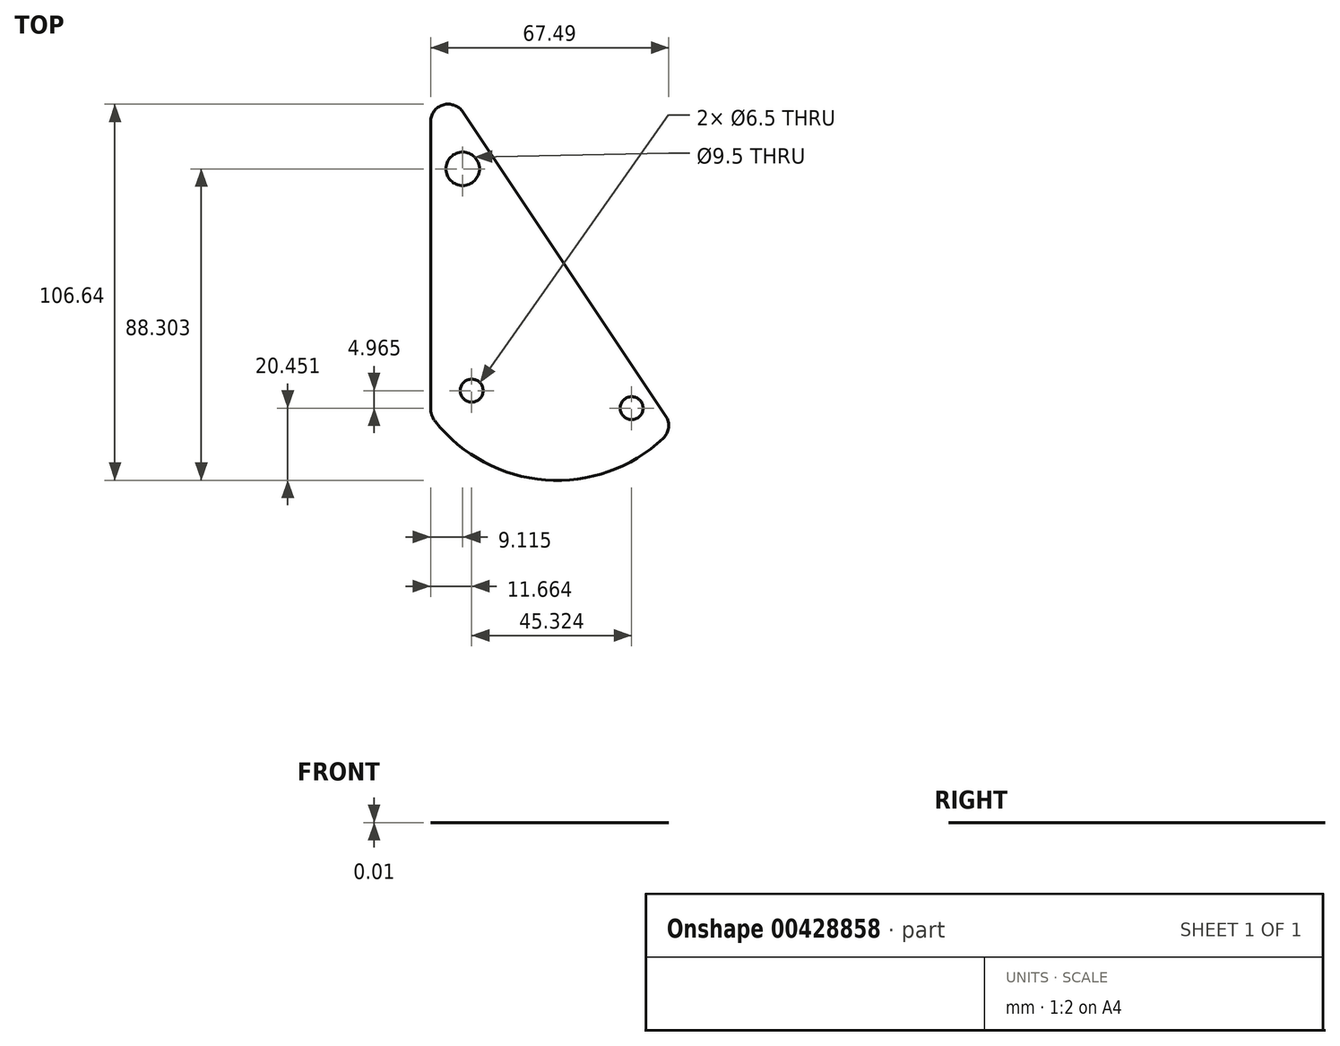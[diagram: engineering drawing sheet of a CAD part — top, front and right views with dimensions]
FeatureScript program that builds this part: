
annotation { "Feature Type Name" : "Feature", "Feature Type Description" : "" }
export const myFeature = defineFeature(function(context is Context, id is Id, definition is map)
    precondition{}
    {
        {
            var Q0;
            Q0=qCreatedBy(makeId("Top.planeOp"),FACE);
            var sketch = newSketch(context, id + "F0", { "sketchPlane" : qUnion([Q0])});
            skLineSegment(sketch, "E0", {"start": v(-32.06, 30.9) * mm, "end": v(-32.06, -50.29) * mm});
            skLineSegment(sketch, "E1", {"start": v(-32.06, -52.29) * mm, "end": v(36.83, -55.8) * mm});
            skLineSegment(sketch, "E2", {"start": v(34.59, -52.45) * mm, "end": v(-22.9, 33.67) * mm});
            skArc(sketch, "E3", {"start": v(-30.76, -54) * mm, "mid": v(0.47, -70.61) * mm, "end": v(33.84, -58.88) * mm});
            skPoint(sketch, "E4.visualSharp", {"position": v(-32.06, -52.29) * mm});
            skArc(sketch, "E4.filletArc", {"start": v(-32.06, -50.29) * mm, "mid": v(-31.72, -52.26) * mm, "end": v(-30.76, -54) * mm});
            skPoint(sketch, "E5.visualSharp", {"position": v(36.83, -55.8) * mm});
            skArc(sketch, "E5.filletArc", {"start": v(33.84, -58.88) * mm, "mid": v(35.4, -55.8) * mm, "end": v(34.59, -52.45) * mm});
            skPoint(sketch, "E6.visualSharp", {"position": v(-32.06, 47.4) * mm});
            skArc(sketch, "E6.filletArc", {"start": v(-22.9, 33.67) * mm, "mid": v(-28.5, 35.68) * mm, "end": v(-32.06, 30.9) * mm});
            skCircle(sketch, "E7", {"center": v(-20.4, -45.32) * mm, "radius": 3.25 * mm});
            skCircle(sketch, "E8", {"center": v(24.93, -50.29) * mm, "radius": 3.25 * mm});
            skCircle(sketch, "E9", {"center": v(-22.95, 17.56) * mm, "radius": 4.75 * mm});
            skSolve(sketch);
        }
        {
            var Q0;
            Q0 = qSketchRegion(id + "F0", true);
            extrude(context, id + "F1", {"entities" : qUnion([Q0]), "depth" : 1 / 101.6 * mm});
        }
    });
